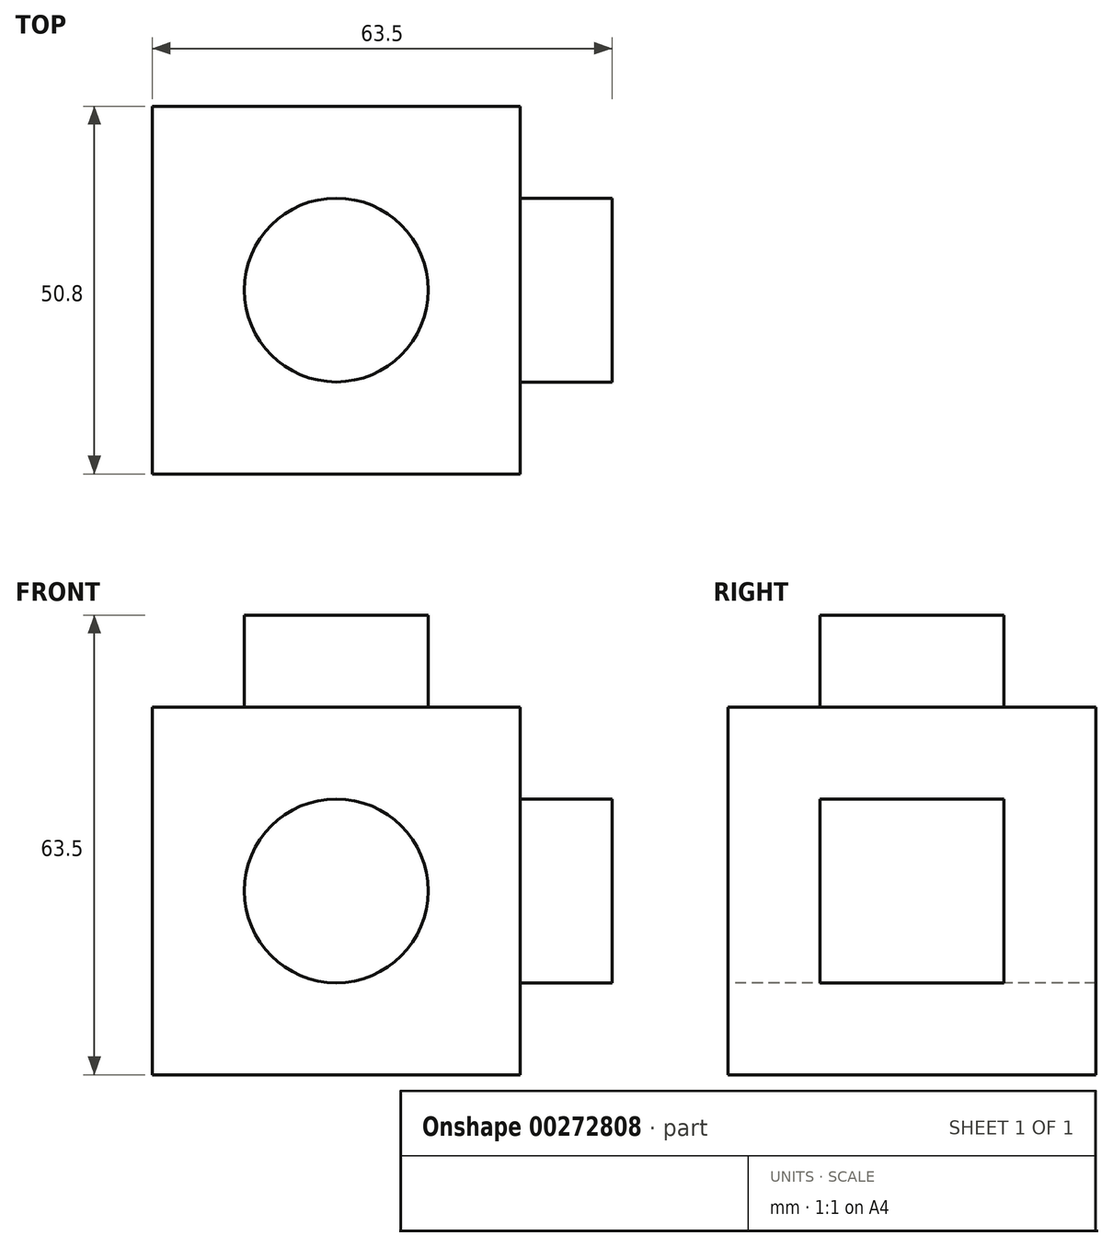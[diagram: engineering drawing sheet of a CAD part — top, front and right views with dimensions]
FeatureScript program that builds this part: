
annotation { "Feature Type Name" : "Feature", "Feature Type Description" : "" }
export const myFeature = defineFeature(function(context is Context, id is Id, definition is map)
    precondition{}
    {
        {
            var Q0;
            Q0=qCreatedBy(makeId("Front.planeOp"),FACE);
            var sketch = newSketch(context, id + "F0", { "sketchPlane" : qUnion([Q0])});
            skLineSegment(sketch, "E0.bottom", {"start": v(0, 0) * mm, "end": v(-50.8, 0) * mm});
            skLineSegment(sketch, "E0.top", {"start": v(0, 50.8) * mm, "end": v(-50.8, 50.8) * mm});
            skLineSegment(sketch, "E0.left", {"start": v(0, 0) * mm, "end": v(0, 50.8) * mm});
            skLineSegment(sketch, "E0.right", {"start": v(-50.8, 0) * mm, "end": v(-50.8, 50.8) * mm});
            skSolve(sketch);
        }
        {
            var Q0;
            Q0=makeQuery(id+"F0.imprint","IMPRINT",FACE,{"disambiguationData":[TD([[makeQuery(id+"F0.imprint","IMPRINT",EDGE,{"derivedFrom":sQuery(id+"F0.wireOp",EDGE,"E0.bottom")}),-1.0]])]});
            extrude(context, id + "F1", {"entities" : qUnion([Q0]), "depth" : 50.8 * mm});
        }
        {
            var Q0;
            Q0=makeQuery(id+"F1.opExtrude","CAP_FACE",FACE,{"disambiguationData":[OSD([sQuery(id+"F0.wireOp",EDGE,"E0.bottom"),sQuery(id+"F0.wireOp",EDGE,"E0.top"),sQuery(id+"F0.wireOp",EDGE,"E0.left"),sQuery(id+"F0.wireOp",EDGE,"E0.right")])],"isStart":false});
            var sketch = newSketch(context, id + "F2", { "sketchPlane" : qUnion([Q0])});
            skCircle(sketch, "E1", {"center": v(-25.4, 25.4) * mm, "radius": 12.7 * mm});
            skSolve(sketch);
        }
        {
            var Q0;
            Q0=makeQuery(id+"F2.imprint","IMPRINT",FACE,{"disambiguationData":[TD([[makeQuery(id+"F2.imprint","IMPRINT",EDGE,{"derivedFrom":sQuery(id+"F2.wireOp",EDGE,"E1")}),1.0]])]});
            extrude(context, id + "F3", {"entities" : qUnion([Q0]), "operationType" : NewBodyOperationType.REMOVE, "oppositeDirection" : true, "depth" : 50.8 * mm});
        }
        {
            var Q0;
            Q0=makeQuery(id+"F1.opExtrude","SWEPT_FACE",FACE,{"disambiguationData":[OSD([sQuery(id+"F0.wireOp",EDGE,"E0.left")])]});
            var sketch = newSketch(context, id + "F4", { "sketchPlane" : qUnion([Q0])});
            skLineSegment(sketch, "E2.bottom", {"start": v(-38.1, 38.1) * mm, "end": v(-12.7, 38.1) * mm});
            skLineSegment(sketch, "E2.top", {"start": v(-38.1, 12.7) * mm, "end": v(-12.7, 12.7) * mm});
            skLineSegment(sketch, "E2.left", {"start": v(-38.1, 38.1) * mm, "end": v(-38.1, 12.7) * mm});
            skLineSegment(sketch, "E2.right", {"start": v(-12.7, 38.1) * mm, "end": v(-12.7, 12.7) * mm});
            skSolve(sketch);
        }
        {
            var Q0;
            Q0 = qSketchRegion(id + "F4", true);
            extrude(context, id + "F5", {"entities" : qUnion([Q0]), "operationType" : NewBodyOperationType.ADD, "depth" : 12.7 * mm});
        }
        {
            var Q0;
            Q0=makeQuery(id+"F1.opExtrude","SWEPT_FACE",FACE,{"disambiguationData":[OSD([sQuery(id+"F0.wireOp",EDGE,"E0.top")])]});
            var sketch = newSketch(context, id + "F6", { "sketchPlane" : qUnion([Q0])});
            skCircle(sketch, "E3", {"center": v(-25.4, -25.4) * mm, "radius": 12.7 * mm});
            skSolve(sketch);
        }
        {
            var Q0;
            Q0=makeQuery(id+"F6.imprint","IMPRINT",FACE,{"disambiguationData":[TD([[makeQuery(id+"F6.imprint","IMPRINT",EDGE,{"derivedFrom":sQuery(id+"F6.wireOp",EDGE,"E3")}),1.0]])]});
            extrude(context, id + "F7", {"entities" : qUnion([Q0]), "operationType" : NewBodyOperationType.ADD, "depth" : 12.7 * mm});
        }
    });
